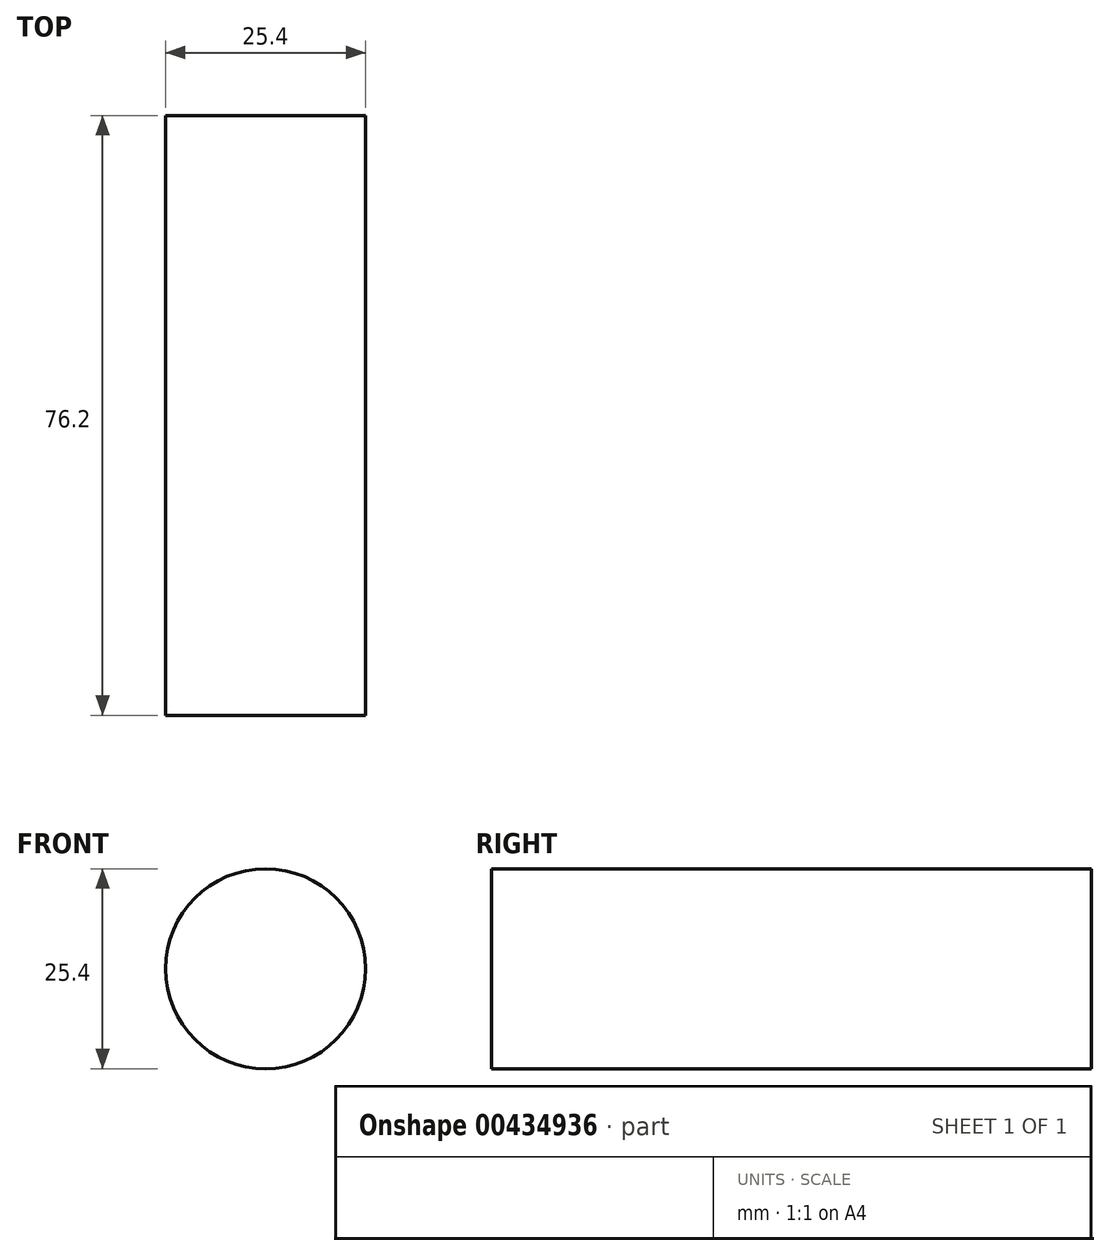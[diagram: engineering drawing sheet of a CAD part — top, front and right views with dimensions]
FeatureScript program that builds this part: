
annotation { "Feature Type Name" : "Feature", "Feature Type Description" : "" }
export const myFeature = defineFeature(function(context is Context, id is Id, definition is map)
    precondition{}
    {
        {
            var Q0;
            Q0=qCreatedBy(makeId("Front.planeOp"),FACE);
            var sketch = newSketch(context, id + "F0", { "sketchPlane" : qUnion([Q0])});
            skCircle(sketch, "E0", {"center": v(-26.22, 21.04) * mm, "radius": 12.7 * mm});
            skSolve(sketch);
        }
        {
            var Q0;
            Q0=makeQuery(id+"F0.imprint","IMPRINT",FACE,{"disambiguationData":[TD([[makeQuery(id+"F0.imprint","IMPRINT",EDGE,{"derivedFrom":sQuery(id+"F0.wireOp",EDGE,"E0")}),1.0]])]});
            extrude(context, id + "F1", {"entities" : qUnion([Q0]), "depth" : 76.2 * mm});
        }
    });
